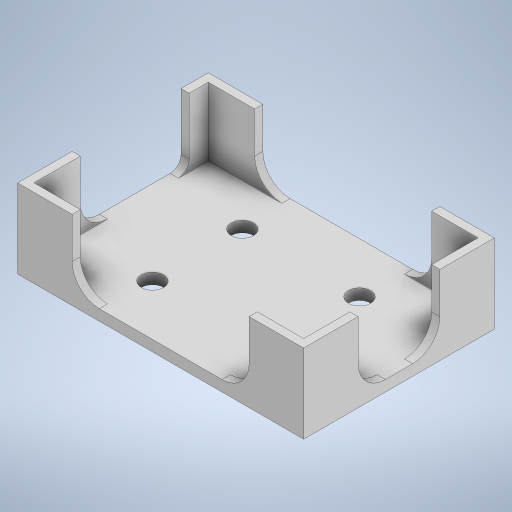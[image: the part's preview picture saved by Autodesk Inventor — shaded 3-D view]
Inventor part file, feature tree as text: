
AUTODESK INVENTOR PART (.ipt)
format: ipt  version: 2024.2 (Build 282272000, 272)  size: 363,008 bytes
history: native  units: mm
features: extrude x5, sketch x5, fillet x2
ambient origin geometry x8: Origin, YZ Plane, XZ Plane, XY Plane, X Axis, Y Axis, Z Axis, Center Point
bodies: Solid1 (feature_tree)
feature tree (12):
  extrude  "Extrusion1"  Depth=48.0mm
  extrude  "Extrusion3"  Depth=4.7mm
  extrude  "Extrusion4"  Depth=4.7mm
  fillet  "Fillet1"  Radius=33.0mm
  extrude  "remove legs"  Depth=7.5mm
  extrude  "Extrusion6"  Depth=4.0mm
  fillet  "Fillet2"  Radius=7.5mm
  sketch  "Sketch1"  dims[d0=58.0mm d1=48.0mm]
  sketch  "Sketch2"  dims[d2=4.7mm d3=4.7mm]
  sketch  "Sketch3"  dims[d4=4.7mm d5=4.7mm d6=33.0mm]
  sketch  "Sketch4"  dims[d7=43.0mm d8=7.5mm]
  sketch  "Sketch5"  dims[d9=7.5mm d10=7.5mm d11=7.5mm d12=7.500001mm d13=7.500001mm d14=10.0mm d15=10.0mm d16=10.0mm d17=10.0mm d18=12.0mm d19=0.0mm d20=105.0mm d21=70.0mm d22=18.5mm d23=31.0mm d26=4.0mm d27=0.0mm d28=20.0mm d37=3.0mm d45=25.0mm d46=0.0mm d47=10.0mm d48=20.0mm d49=3.0mm d50=3.0mm d51=3.0mm d52=3.0mm d53=20.0mm d54=20.0mm d55=20.0mm d56=20.0mm d57=3.0mm d58=3.0mm d59=100.0mm d60=15.0mm d61=25.0mm d62=0.0mm d63=8.2mm d64=8.2mm d65=8.2mm d66=8.2mm d67=4.0mm d68=0.0mm d69=10.0mm d70=7.0mm d71=4.0mm]
